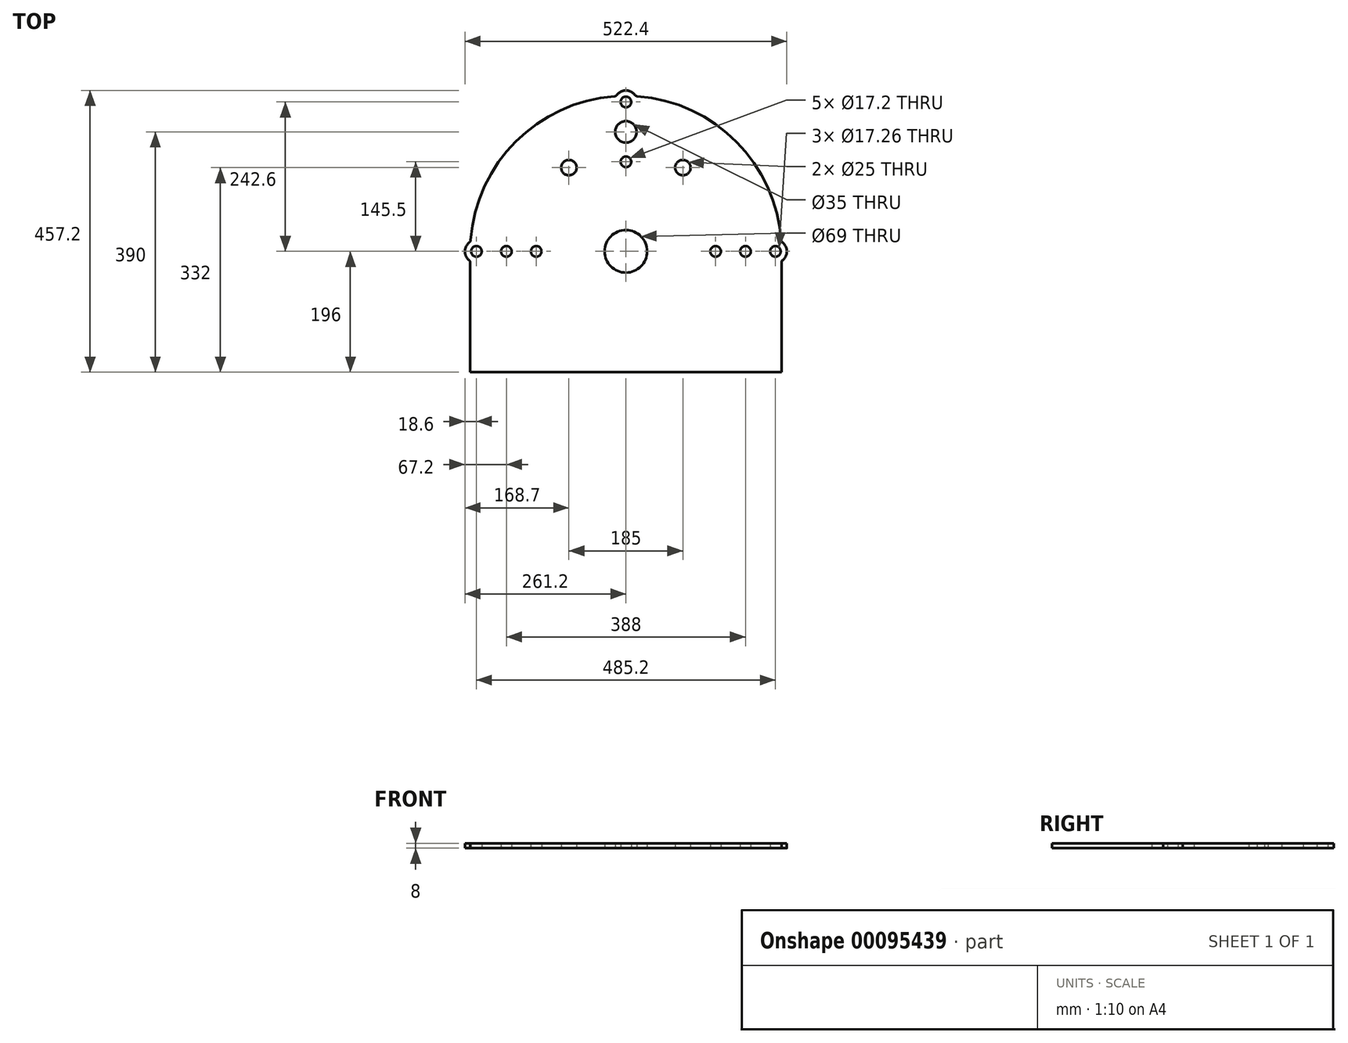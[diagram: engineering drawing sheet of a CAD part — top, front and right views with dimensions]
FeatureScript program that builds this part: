
annotation { "Feature Type Name" : "Feature", "Feature Type Description" : "" }
export const myFeature = defineFeature(function(context is Context, id is Id, definition is map)
    precondition{}
    {
        {
            var Q0;
            Q0=qCreatedBy(makeId("Top.planeOp"),FACE);
            var sketch = newSketch(context, id + "F0", { "sketchPlane" : qUnion([Q0])});
            skArc(sketch, "E0", {"start": v(14.85, 221.2) * mm, "mid": v(16.45, 219.82) * mm, "end": v(18.48, 219.22) * mm});
            skArc(sketch, "E1", {"start": v(-18.48, 219.22) * mm, "mid": v(-16.45, 219.82) * mm, "end": v(-14.85, 221.2) * mm});
            skArc(sketch, "E2", {"start": v(-253.8, -17.75) * mm, "mid": v(-252.42, -16.15) * mm, "end": v(-251.82, -14.12) * mm});
            skArc(sketch, "E3", {"start": v(-252.5, -50.9) * mm, "mid": v(-252.98, -48.76) * mm, "end": v(-254.34, -47.02) * mm});
            skArc(sketch, "E4", {"start": v(251.99, -16.54) * mm, "mid": v(179.4, 145.08) * mm, "end": v(18.48, 219.22) * mm});
            skArc(sketch, "E5", {"start": v(14.85, 221.2) * mm, "mid": v(0, 228.6) * mm, "end": v(-14.85, 221.2) * mm});
            skArc(sketch, "E6", {"start": v(-18.48, 219.22) * mm, "mid": v(-178.54, 145.94) * mm, "end": v(-251.82, -14.12) * mm});
            skArc(sketch, "E7", {"start": v(-253.8, -17.75) * mm, "mid": v(-261.2, -32.25) * mm, "end": v(-254.34, -47.02) * mm});
            skLineSegment(sketch, "E8", {"start": v(-252.5, -50.9) * mm, "end": v(-252.5, -228.6) * mm});
            skArc(sketch, "E9", {"start": v(252.5, -48.35) * mm, "mid": v(261.2, -32.3) * mm, "end": v(251.99, -16.54) * mm});
            skLineSegment(sketch, "E10", {"start": v(252.5, -228.6) * mm, "end": v(252.5, -48.35) * mm});
            skLineSegment(sketch, "E11", {"start": v(252.5, -228.6) * mm, "end": v(-252.5, -228.6) * mm});
            skCircle(sketch, "E12", {"center": v(-194, -32.6) * mm, "radius": 8.6 * mm});
            skCircle(sketch, "E13", {"center": v(145.5, -32.6) * mm, "radius": 8.6 * mm});
            skCircle(sketch, "E14", {"center": v(194, -32.6) * mm, "radius": 8.6 * mm});
            skCircle(sketch, "E15", {"center": v(0, 112.9) * mm, "radius": 8.6 * mm});
            skCircle(sketch, "E16", {"center": v(-145.5, -32.6) * mm, "radius": 8.6 * mm});
            skCircle(sketch, "E17", {"center": v(92.5, 103.4) * mm, "radius": 12.5 * mm});
            skCircle(sketch, "E18", {"center": v(-92.5, 103.4) * mm, "radius": 12.5 * mm});
            skCircle(sketch, "E19", {"center": v(242.6, -32.6) * mm, "radius": 8.63 * mm});
            skCircle(sketch, "E20", {"center": v(0, 210) * mm, "radius": 8.63 * mm});
            skCircle(sketch, "E21", {"center": v(-242.6, -32.6) * mm, "radius": 8.63 * mm});
            skCircle(sketch, "E22", {"center": v(0, 161.4) * mm, "radius": 17.5 * mm});
            skCircle(sketch, "E23", {"center": v(0, -32.6) * mm, "radius": 34.5 * mm});
            skSolve(sketch);
        }
        {
            var Q0;
            Q0 = qSketchRegion(id + "F0", true);
            extrude(context, id + "F1", {"entities" : qUnion([Q0]), "depth" : 8 * mm});
        }
    });
